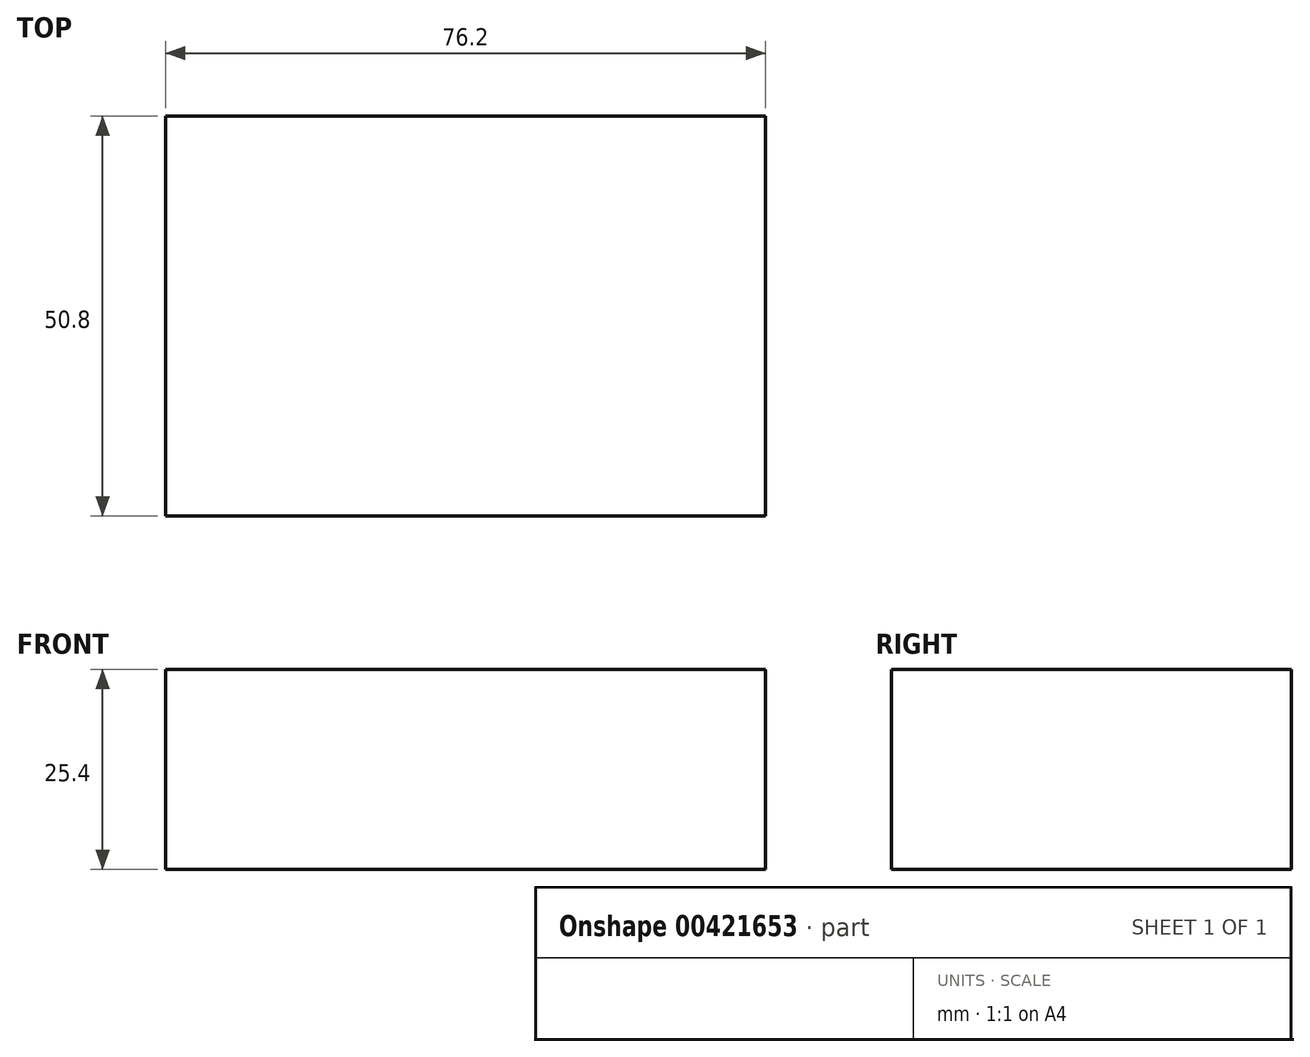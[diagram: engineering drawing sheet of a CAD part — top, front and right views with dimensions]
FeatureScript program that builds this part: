
annotation { "Feature Type Name" : "Feature", "Feature Type Description" : "" }
export const myFeature = defineFeature(function(context is Context, id is Id, definition is map)
    precondition{}
    {
        {
            var Q0;
            Q0=qCreatedBy(makeId("Top.planeOp"),FACE);
            var sketch = newSketch(context, id + "F0", { "sketchPlane" : qUnion([Q0])});
            skLineSegment(sketch, "E0.bottom", {"start": v(0, 0) * mm, "end": v(76.2, 0) * mm});
            skLineSegment(sketch, "E0.top", {"start": v(0, 50.8) * mm, "end": v(76.2, 50.8) * mm});
            skLineSegment(sketch, "E0.left", {"start": v(0, 0) * mm, "end": v(0, 50.8) * mm});
            skLineSegment(sketch, "E0.right", {"start": v(76.2, 0) * mm, "end": v(76.2, 50.8) * mm});
            skSolve(sketch);
        }
        {
            var Q0;
            Q0 = qSketchRegion(id + "F0", true);
            extrude(context, id + "F1", {"entities" : qUnion([Q0]), "depth" : 25.4 * mm});
        }
    });
